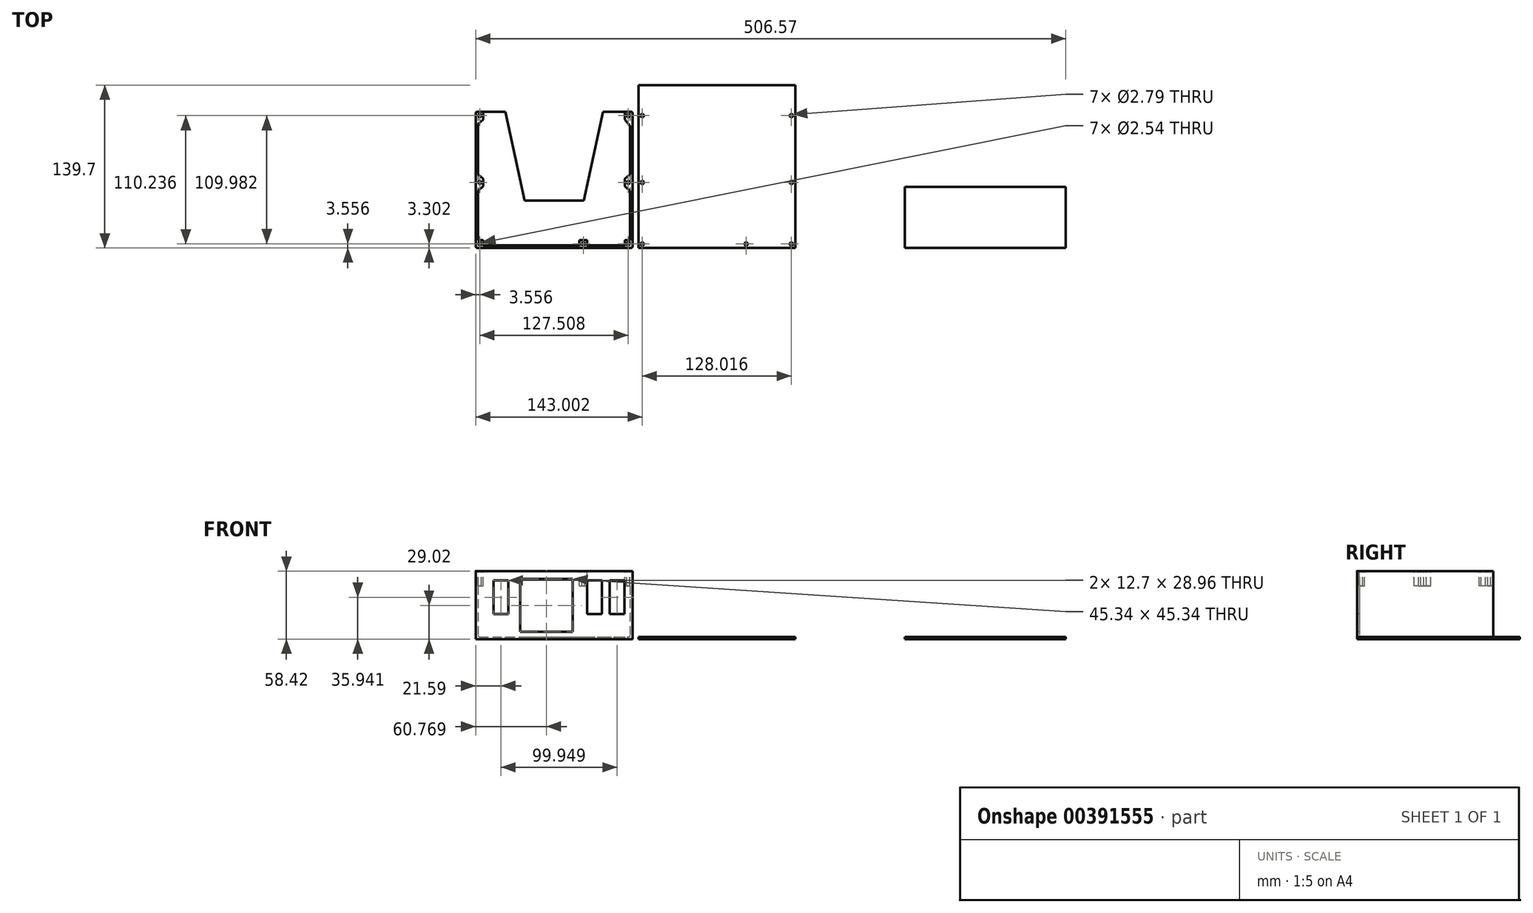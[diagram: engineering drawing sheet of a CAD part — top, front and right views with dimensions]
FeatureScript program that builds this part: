
annotation { "Feature Type Name" : "Feature", "Feature Type Description" : "" }
export const myFeature = defineFeature(function(context is Context, id is Id, definition is map)
    precondition{}
    {
        {
            var Q0;
            Q0=qCreatedBy(makeId("Top.planeOp"),FACE);
            var sketch = newSketch(context, id + "F0", { "sketchPlane" : qUnion([Q0])});
            skLineSegment(sketch, "E0.bottom", {"start": v(-137.16, -2.54) * mm, "end": v(-2.54, -2.54) * mm});
            skLineSegment(sketch, "E0.top", {"start": v(-137.16, -119.38) * mm, "end": v(-2.54, -119.38) * mm});
            skLineSegment(sketch, "E0.left", {"start": v(-137.16, -2.54) * mm, "end": v(-137.16, -119.38) * mm});
            skLineSegment(sketch, "E0.right", {"start": v(-2.54, -2.54) * mm, "end": v(-2.54, -119.38) * mm});
            skSolve(sketch);
        }
        {
            var Q0;
            Q0 = qSketchRegion(id + "F0", true);
            extrude(context, id + "F1", {"entities" : qUnion([Q0]), "depth" : 58.42 * mm});
        }
        {
            var Q0;
            Q0=makeQuery(id+"F1.opExtrude","CAP_FACE",FACE,{"disambiguationData":[OSD([sQuery(id+"F0.wireOp",EDGE,"E0.bottom"),sQuery(id+"F0.wireOp",EDGE,"E0.top"),sQuery(id+"F0.wireOp",EDGE,"E0.left"),sQuery(id+"F0.wireOp",EDGE,"E0.right")])],"isStart":false});
            shell(context, id + "F2", {"entities" : qUnion([Q0]), "thickness" : 2.03 * mm});
        }
        {
            var Q0;
            Q0=makeQuery(id+"F2.opShell","OFFSET_FACE",FACE,{"disambiguationData":[OSD([sQuery(id+"F0.wireOp",EDGE,"E0.bottom")])]});
            extrude(context, id + "F3", {"entities" : qUnion([Q0]), "operationType" : NewBodyOperationType.REMOVE, "endBound" : BoundingType.UP_TO_NEXT, "oppositeDirection" : true, "depth" : 25.4 * mm});
        }
        {
            var Q0;
            Q0=makeQuery(id+"F1.opExtrude","SWEPT_FACE",FACE,{"disambiguationData":[OSD([sQuery(id+"F0.wireOp",EDGE,"E0.top")])]});
            var sketch = newSketch(context, id + "F4", { "sketchPlane" : qUnion([Q0])});
            skLineSegment(sketch, "E1.bottom", {"start": v(-99.06, 51.69) * mm, "end": v(-53.72, 51.69) * mm});
            skLineSegment(sketch, "E1.top", {"start": v(-99.06, 6.35) * mm, "end": v(-53.72, 6.35) * mm});
            skLineSegment(sketch, "E1.left", {"start": v(-99.06, 51.69) * mm, "end": v(-99.06, 6.35) * mm});
            skLineSegment(sketch, "E1.right", {"start": v(-53.72, 51.69) * mm, "end": v(-53.72, 6.35) * mm});
            skLineSegment(sketch, "E2.bottom", {"start": v(-41.4, 50.42) * mm, "end": v(-28.7, 50.42) * mm});
            skLineSegment(sketch, "E2.top", {"start": v(-41.4, 21.46) * mm, "end": v(-28.7, 21.46) * mm});
            skLineSegment(sketch, "E2.left", {"start": v(-41.4, 50.42) * mm, "end": v(-41.4, 21.46) * mm});
            skLineSegment(sketch, "E2.right", {"start": v(-28.7, 50.42) * mm, "end": v(-28.7, 21.46) * mm});
            skLineSegment(sketch, "E3.bottom", {"start": v(-21.97, 50.42) * mm, "end": v(-9.27, 50.42) * mm});
            skLineSegment(sketch, "E3.top", {"start": v(-21.97, 21.46) * mm, "end": v(-9.27, 21.46) * mm});
            skLineSegment(sketch, "E3.left", {"start": v(-21.97, 50.42) * mm, "end": v(-21.97, 21.46) * mm});
            skLineSegment(sketch, "E3.right", {"start": v(-9.27, 50.42) * mm, "end": v(-9.27, 21.46) * mm});
            skLineSegment(sketch, "E4.bottom", {"start": v(-121.92, 50.42) * mm, "end": v(-109.22, 50.42) * mm});
            skLineSegment(sketch, "E4.top", {"start": v(-121.92, 21.46) * mm, "end": v(-109.22, 21.46) * mm});
            skLineSegment(sketch, "E4.left", {"start": v(-121.92, 50.42) * mm, "end": v(-121.92, 21.46) * mm});
            skLineSegment(sketch, "E4.right", {"start": v(-109.22, 50.42) * mm, "end": v(-109.22, 21.46) * mm});
            skSolve(sketch);
        }
        {
            var Q0;
            Q0 = qSketchRegion(id + "F4", true);
            extrude(context, id + "F5", {"entities" : qUnion([Q0]), "operationType" : NewBodyOperationType.REMOVE, "endBound" : BoundingType.UP_TO_NEXT, "oppositeDirection" : true, "depth" : 25.4 * mm});
        }
        {
            var Q0;
            Q0=makeQuery(id+"F1.opExtrude","CAP_FACE",FACE,{"disambiguationData":[OSD([sQuery(id+"F0.wireOp",EDGE,"E0.bottom"),sQuery(id+"F0.wireOp",EDGE,"E0.top"),sQuery(id+"F0.wireOp",EDGE,"E0.left"),sQuery(id+"F0.wireOp",EDGE,"E0.right")])],"isStart":false});
            var sketch = newSketch(context, id + "F6", { "sketchPlane" : qUnion([Q0])});
            skLineSegment(sketch, "E5.bottom", {"start": v(-4.57, -117.35) * mm, "end": v(-9.14, -117.35) * mm});
            skLineSegment(sketch, "E5.top", {"start": v(-4.57, -112.78) * mm, "end": v(-9.14, -112.78) * mm});
            skLineSegment(sketch, "E5.left", {"start": v(-4.57, -117.35) * mm, "end": v(-4.57, -112.78) * mm});
            skLineSegment(sketch, "E5.right", {"start": v(-9.14, -117.35) * mm, "end": v(-9.14, -112.78) * mm});
            skLineSegment(sketch, "E6.bottom", {"start": v(-135.13, -117.35) * mm, "end": v(-130.56, -117.35) * mm});
            skLineSegment(sketch, "E6.top", {"start": v(-135.13, -112.78) * mm, "end": v(-130.56, -112.78) * mm});
            skLineSegment(sketch, "E6.left", {"start": v(-135.13, -117.35) * mm, "end": v(-135.13, -112.78) * mm});
            skLineSegment(sketch, "E6.right", {"start": v(-130.56, -117.35) * mm, "end": v(-130.56, -112.78) * mm});
            skLineSegment(sketch, "E7.right", {"start": v(-9.14, -66.55) * mm, "end": v(-9.14, -59.94) * mm});
            skLineSegment(sketch, "E8.right", {"start": v(-130.56, -66.55) * mm, "end": v(-130.56, -59.94) * mm});
            skLineSegment(sketch, "E9", {"start": v(-9.14, -66.55) * mm, "end": v(-4.57, -70.38) * mm});
            skLineSegment(sketch, "E10", {"start": v(-4.57, -70.38) * mm, "end": v(-4.57, -56.1) * mm});
            skLineSegment(sketch, "E11", {"start": v(-9.14, -59.94) * mm, "end": v(-4.57, -56.1) * mm});
            skLineSegment(sketch, "E12", {"start": v(-135.13, -70.38) * mm, "end": v(-130.56, -66.55) * mm});
            skLineSegment(sketch, "E13", {"start": v(-130.56, -59.94) * mm, "end": v(-135.13, -56.1) * mm});
            skLineSegment(sketch, "E14", {"start": v(-135.13, -70.38) * mm, "end": v(-135.13, -56.1) * mm});
            skCircle(sketch, "E15", {"center": v(-6.1, -63.25) * mm, "radius": 1.27 * mm});
            skPoint(sketch, "E15.centerSnap0", {"position": v(-9.14, -63.25) * mm});
            skCircle(sketch, "E16", {"center": v(-133.6, -63.25) * mm, "radius": 1.27 * mm});
            skPoint(sketch, "E16.centerSnap0", {"position": v(-130.56, -63.25) * mm});
            skCircle(sketch, "E17", {"center": v(-133.6, -115.82) * mm, "radius": 1.27 * mm});
            skCircle(sketch, "E18", {"center": v(-6.1, -115.82) * mm, "radius": 1.27 * mm});
            skLineSegment(sketch, "E19", {"start": v(-4.57, -2.54) * mm, "end": v(-9.14, -2.54) * mm});
            skLineSegment(sketch, "E20", {"start": v(-9.14, -2.54) * mm, "end": v(-9.14, -9.14) * mm});
            skLineSegment(sketch, "E21", {"start": v(-9.14, -9.14) * mm, "end": v(-4.57, -14.6) * mm});
            skLineSegment(sketch, "E22", {"start": v(-135.13, -2.54) * mm, "end": v(-130.56, -2.54) * mm});
            skLineSegment(sketch, "E23", {"start": v(-130.56, -2.54) * mm, "end": v(-130.56, -9.14) * mm});
            skLineSegment(sketch, "E24", {"start": v(-130.56, -9.14) * mm, "end": v(-135.13, -12.98) * mm});
            skLineSegment(sketch, "E25", {"start": v(-135.13, -12.98) * mm, "end": v(-135.13, -2.54) * mm});
            skLineSegment(sketch, "E26", {"start": v(-4.57, -14.6) * mm, "end": v(-4.57, -2.54) * mm});
            skCircle(sketch, "E27", {"center": v(-133.6, -5.84) * mm, "radius": 1.27 * mm});
            skPoint(sketch, "E27.centerSnap0", {"position": v(-130.56, -5.84) * mm});
            skCircle(sketch, "E28", {"center": v(-6.1, -5.84) * mm, "radius": 1.27 * mm});
            skLineSegment(sketch, "E29.bottom", {"start": v(-48, -117.35) * mm, "end": v(-41.4, -117.35) * mm});
            skLineSegment(sketch, "E29.top", {"start": v(-48, -112.78) * mm, "end": v(-41.4, -112.78) * mm});
            skLineSegment(sketch, "E29.left", {"start": v(-48, -117.35) * mm, "end": v(-48, -112.78) * mm});
            skLineSegment(sketch, "E29.right", {"start": v(-41.4, -117.35) * mm, "end": v(-41.4, -112.78) * mm});
            skCircle(sketch, "E30", {"center": v(-44.7, -115.82) * mm, "radius": 1.27 * mm});
            skPoint(sketch, "E30.centerSnap0", {"position": v(-44.7, -117.35) * mm});
            skSolve(sketch);
        }
        {
            var Q0;
            Q0 = qSketchRegion(id + "F6", true);
            extrude(context, id + "F7", {"entities" : qUnion([Q0]), "operationType" : NewBodyOperationType.ADD, "oppositeDirection" : true, "depth" : 12.7 * mm});
        }
        {
            var Q0;
            Q0=qCreatedBy(makeId("Top.planeOp"),FACE);
            var sketch = newSketch(context, id + "F8", { "sketchPlane" : qUnion([Q0])});
            skLineSegment(sketch, "E31.bottom", {"start": v(137.16, 20.32) * mm, "end": v(2.54, 20.32) * mm});
            skLineSegment(sketch, "E31.top", {"start": v(137.16, -119.38) * mm, "end": v(2.54, -119.38) * mm});
            skLineSegment(sketch, "E31.left", {"start": v(137.16, 20.32) * mm, "end": v(137.16, -119.38) * mm});
            skLineSegment(sketch, "E31.right", {"start": v(2.54, 20.32) * mm, "end": v(2.54, -119.38) * mm});
            skCircle(sketch, "E32", {"center": v(133.86, -116.08) * mm, "radius": 1.4 * mm});
            skCircle(sketch, "E33", {"center": v(5.84, -116.08) * mm, "radius": 1.4 * mm});
            skCircle(sketch, "E34", {"center": v(5.84, -5.84) * mm, "radius": 1.4 * mm});
            skCircle(sketch, "E35", {"center": v(133.86, -5.84) * mm, "radius": 1.4 * mm});
            skCircle(sketch, "E36", {"center": v(133.86, -63.25) * mm, "radius": 1.4 * mm});
            skCircle(sketch, "E37", {"center": v(5.84, -63.25) * mm, "radius": 1.4 * mm});
            skCircle(sketch, "E38", {"center": v(95, -116.08) * mm, "radius": 1.4 * mm});
            skLineSegment(sketch, "E39.bottom", {"start": v(231.14, -119.38) * mm, "end": v(369.4, -119.38) * mm});
            skLineSegment(sketch, "E39.top", {"start": v(231.14, -66.99) * mm, "end": v(369.4, -66.99) * mm});
            skLineSegment(sketch, "E39.left", {"start": v(231.14, -119.38) * mm, "end": v(231.14, -66.99) * mm});
            skLineSegment(sketch, "E39.right", {"start": v(369.4, -119.38) * mm, "end": v(369.4, -66.99) * mm});
            skSolve(sketch);
        }
        {
            var Q0;
            Q0 = qSketchRegion(id + "F8", true);
            extrude(context, id + "F9", {"entities" : qUnion([Q0]), "depth" : 2.03 * mm});
        }
        {
            var Q0;
            Q0=makeQuery(id+"F1.opExtrude","SWEPT_EDGE",EDGE,{"disambiguationData":[OSD([sQuery(id+"F0.wireOp",EDGE,"E0.top"),sQuery(id+"F0.wireOp",EDGE,"E0.left")])]});
            var Q1;
            Q1=makeQuery(id+"F1.opExtrude","SWEPT_EDGE",EDGE,{"disambiguationData":[OSD([sQuery(id+"F0.wireOp",EDGE,"E0.bottom"),sQuery(id+"F0.wireOp",EDGE,"E0.left")])]});
            var Q2;
            Q2=makeQuery(id+"F1.opExtrude","SWEPT_EDGE",EDGE,{"disambiguationData":[OSD([sQuery(id+"F0.wireOp",EDGE,"E0.top"),sQuery(id+"F0.wireOp",EDGE,"E0.right")])]});
            var Q3;
            Q3=makeQuery(id+"F1.opExtrude","SWEPT_EDGE",EDGE,{"disambiguationData":[OSD([sQuery(id+"F0.wireOp",EDGE,"E0.bottom"),sQuery(id+"F0.wireOp",EDGE,"E0.right")])]});
            fillet(context, id + "F10", {"entities" : qUnion([Q0, Q1, Q2, Q3]), "radius" : 1.27 * mm, "tangentPropagation" : true, "allowEdgeOverflow" : false});
        }
        {
            var Q0;
            {var subQ0=sQuery(id+"F0.wireOp",EDGE,"E0.left");var subQ1=sQuery(id+"F0.wireOp",EDGE,"E0.bottom");Q0=makeQuery(id+"F3.boolean.opBoolean","MERGE",EDGE,{"derivedFrom":[makeQuery(id+"F2.opShell","OFFSET_EDGE",EDGE,{"disambiguationData":[OSD([subQ0]),TDD([makeQuery(id+"F1.opExtrude","CAP_EDGE",EDGE,{"disambiguationData":[OSD([subQ0])],"isStart":true})])]}),makeQuery(id+"F3.opExtrude","SWEPT_EDGE",EDGE,{"disambiguationData":[OSD([subQ1,subQ0]),TDD([makeQuery(id+"F2.opShell","OFFSET_VERTEX",VERTEX,{"disambiguationData":[OSD([subQ1,subQ0]),TDD([makeQuery(id+"F1.opExtrude","CAP_VERTEX",VERTEX,{"disambiguationData":[OSD([subQ1,subQ0])],"isStart":true})])]})])]})]});}
            var Q1;
            {var subQ0=sQuery(id+"F0.wireOp",EDGE,"E0.top");Q1=makeQuery(id+"F2.opShell","OFFSET_EDGE",EDGE,{"disambiguationData":[OSD([subQ0]),TDD([makeQuery(id+"F1.opExtrude","CAP_EDGE",EDGE,{"disambiguationData":[OSD([subQ0])],"isStart":true})])]});}
            var Q2;
            Q2=makeQuery(id+"F2.opShell","OFFSET_EDGE",EDGE,{"disambiguationData":[OSD([sQuery(id+"F0.wireOp",EDGE,"E0.top"),sQuery(id+"F0.wireOp",EDGE,"E0.left")])]});
            var Q3;
            Q3=makeQuery(id+"F2.opShell","OFFSET_EDGE",EDGE,{"disambiguationData":[OSD([sQuery(id+"F0.wireOp",EDGE,"E0.top"),sQuery(id+"F0.wireOp",EDGE,"E0.right")])]});
            var Q4;
            {var subQ0=sQuery(id+"F0.wireOp",EDGE,"E0.right");var subQ1=sQuery(id+"F0.wireOp",EDGE,"E0.bottom");Q4=makeQuery(id+"F3.boolean.opBoolean","MERGE",EDGE,{"derivedFrom":[makeQuery(id+"F2.opShell","OFFSET_EDGE",EDGE,{"disambiguationData":[OSD([subQ0]),TDD([makeQuery(id+"F1.opExtrude","CAP_EDGE",EDGE,{"disambiguationData":[OSD([subQ0])],"isStart":true})])]}),makeQuery(id+"F3.opExtrude","SWEPT_EDGE",EDGE,{"disambiguationData":[OSD([subQ1,subQ0]),TDD([makeQuery(id+"F2.opShell","OFFSET_VERTEX",VERTEX,{"disambiguationData":[OSD([subQ1,subQ0]),TDD([makeQuery(id+"F1.opExtrude","CAP_VERTEX",VERTEX,{"disambiguationData":[OSD([subQ1,subQ0])],"isStart":true})])]})])]})]});}
            fillet(context, id + "F11", {"entities" : qUnion([Q0, Q1, Q2, Q3, Q4]), "radius" : 1.27 * mm, "tangentPropagation" : true, "allowEdgeOverflow" : false});
        }
        {
            var Q0;
            {var subQ0=sQuery(id+"F0.wireOp",EDGE,"E0.bottom");Q0=makeQuery(id+"F3.boolean.opBoolean","MERGE",FACE,{"derivedFrom":[makeQuery(id+"F2.opShell","OFFSET_FACE",FACE,{"disambiguationData":[OSD([subQ0,sQuery(id+"F0.wireOp",EDGE,"E0.top"),sQuery(id+"F0.wireOp",EDGE,"E0.left"),sQuery(id+"F0.wireOp",EDGE,"E0.right")])]}),makeQuery(id+"F3.opExtrude","SWEPT_FACE",FACE,{"disambiguationData":[OSD([subQ0]),TDD([makeQuery(id+"F2.opShell","OFFSET_EDGE",EDGE,{"disambiguationData":[OSD([subQ0]),TDD([makeQuery(id+"F1.opExtrude","CAP_EDGE",EDGE,{"disambiguationData":[OSD([subQ0])],"isStart":true})])]})])]})]});}
            var sketch = newSketch(context, id + "F12", { "sketchPlane" : qUnion([Q0])});
            skLineSegment(sketch, "E40", {"start": v(-111.76, -2.54) * mm, "end": v(-95.25, -78.74) * mm});
            skLineSegment(sketch, "E41", {"start": v(-95.25, -78.74) * mm, "end": v(-44.45, -78.74) * mm});
            skLineSegment(sketch, "E42", {"start": v(-44.45, -78.74) * mm, "end": v(-27.94, -2.54) * mm});
            skLineSegment(sketch, "E43", {"start": v(-27.94, -2.54) * mm, "end": v(-111.76, -2.54) * mm});
            skSolve(sketch);
        }
        {
            var Q0;
            Q0 = qSketchRegion(id + "F12", true);
            extrude(context, id + "F13", {"entities" : qUnion([Q0]), "operationType" : NewBodyOperationType.REMOVE, "endBound" : BoundingType.UP_TO_NEXT, "oppositeDirection" : true, "depth" : 25.4 * mm});
        }
    });
